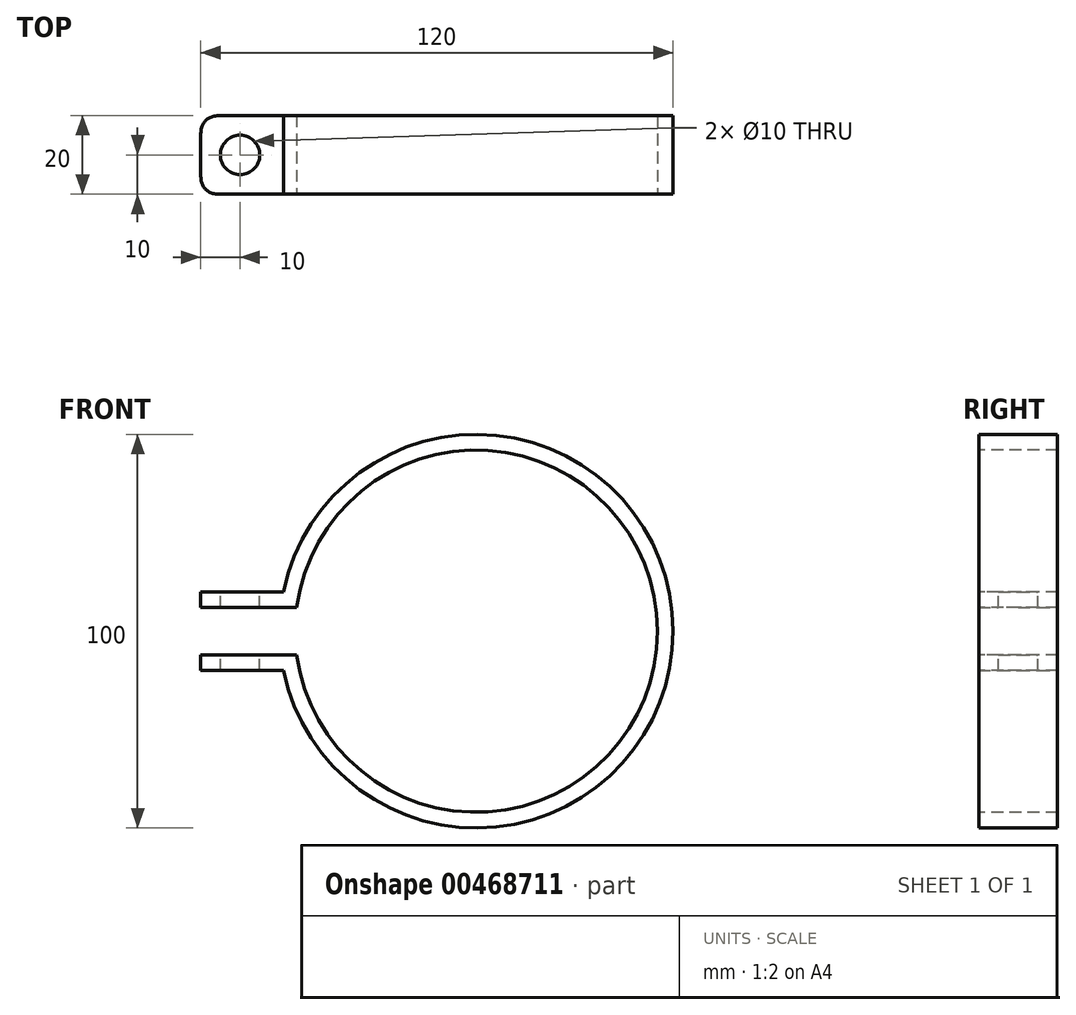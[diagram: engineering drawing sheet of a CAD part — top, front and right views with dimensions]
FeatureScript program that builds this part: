
annotation { "Feature Type Name" : "Feature", "Feature Type Description" : "" }
export const myFeature = defineFeature(function(context is Context, id is Id, definition is map)
    precondition{}
    {
        {
            var Q0;
            Q0=qCreatedBy(makeId("Front.planeOp"),FACE);
            var sketch = newSketch(context, id + "F0", { "sketchPlane" : qUnion([Q0])});
            skArc(sketch, "E0", {"start": v(-48.99, -10) * mm, "mid": v(50, 0) * mm, "end": v(-48.99, 10) * mm});
            skLineSegment(sketch, "E1", {"start": v(-70, 10) * mm, "end": v(-48.99, 10) * mm});
            skLineSegment(sketch, "E2", {"start": v(-70, -10) * mm, "end": v(-48.99, -10) * mm});
            skLineSegment(sketch, "E3.0", {"start": v(-70, 6) * mm, "end": v(-45.6, 6) * mm});
            skArc(sketch, "E3.1", {"start": v(-45.6, -6) * mm, "mid": v(46, 0) * mm, "end": v(-45.6, 6) * mm});
            skLineSegment(sketch, "E4", {"start": v(-70, 10) * mm, "end": v(-70, 6) * mm});
            skLineSegment(sketch, "E5", {"start": v(-70, -6) * mm, "end": v(-70, -10) * mm});
            skLineSegment(sketch, "E6", {"start": v(-70, -6) * mm, "end": v(-45.6, -6) * mm});
            skSolve(sketch);
        }
        {
            var Q0;
            Q0=makeQuery(id+"F0.imprint","IMPRINT",FACE,{"disambiguationData":[TD([[makeQuery(id+"F0.imprint","IMPRINT",EDGE,{"derivedFrom":sQuery(id+"F0.wireOp",EDGE,"E0")}),1.0]])]});
            extrude(context, id + "F1", {"entities" : qUnion([Q0]), "endBound" : BoundingType.SYMMETRIC, "oppositeDirection" : true, "depth" : 20 * mm});
        }
        {
            var Q0;
            Q0=makeQuery(id+"F1.opExtrude","CAP_EDGE",EDGE,{"disambiguationData":[OSD([sQuery(id+"F0.wireOp",EDGE,"E4")])],"isStart":false});
            var Q1;
            Q1=makeQuery(id+"F1.opExtrude","CAP_EDGE",EDGE,{"disambiguationData":[OSD([sQuery(id+"F0.wireOp",EDGE,"E5")])],"isStart":false});
            var Q2;
            Q2=makeQuery(id+"F1.opExtrude","CAP_EDGE",EDGE,{"disambiguationData":[OSD([sQuery(id+"F0.wireOp",EDGE,"E5")])],"isStart":true});
            var Q3;
            Q3=makeQuery(id+"F1.opExtrude","CAP_EDGE",EDGE,{"disambiguationData":[OSD([sQuery(id+"F0.wireOp",EDGE,"E4")])],"isStart":true});
            fillet(context, id + "F2", {"entities" : qUnion([Q0, Q1, Q2, Q3]), "radius" : 5 * mm, "tangentPropagation" : true, "rho" : 0.5, "crossSection" : FilletCrossSection.CONIC, "allowEdgeOverflow" : false});
        }
        {
            var Q0;
            Q0=makeQuery(id+"F1.opExtrude","SWEPT_FACE",FACE,{"disambiguationData":[OSD([sQuery(id+"F0.wireOp",EDGE,"E1")])]});
            var sketch = newSketch(context, id + "F3", { "sketchPlane" : qUnion([Q0])});
            skCircle(sketch, "E7", {"center": v(-60, 0) * mm, "radius": 5 * mm});
            skPoint(sketch, "E7.centerSnap0", {"position": v(-48.99, 0) * mm});
            skSolve(sketch);
        }
        {
            var Q0;
            Q0=makeQuery(id+"F3.imprint","IMPRINT",FACE,{"disambiguationData":[TD([[makeQuery(id+"F3.imprint","IMPRINT",EDGE,{"derivedFrom":sQuery(id+"F3.wireOp",EDGE,"E7")}),1.0]])]});
            extrude(context, id + "F4", {"entities" : qUnion([Q0]), "operationType" : NewBodyOperationType.REMOVE, "oppositeDirection" : true, "depth" : 25.4 * mm});
        }
    });
